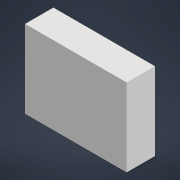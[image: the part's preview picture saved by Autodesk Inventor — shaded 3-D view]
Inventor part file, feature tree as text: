
AUTODESK INVENTOR PART (.ipt)
format: ipt  version: 2022 (Build 260153070, 153G)  size: 83,968 bytes
history: native  units: mm
features: other x1, extrude x1, sketch x1
ambient origin geometry x8: Origin, YZ Plane, XZ Plane, XY Plane, X Axis, Y Axis, Z Axis, Center Point
bodies: Body1 (feature_tree)
feature tree (3):
  other  "Твердое тело1"
  extrude  "Выдавливание1"  Depth=218.0mm
  sketch  "Эскиз1"
